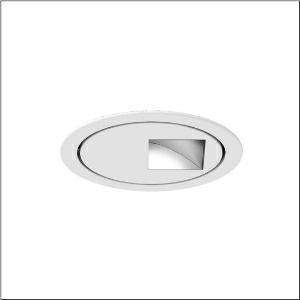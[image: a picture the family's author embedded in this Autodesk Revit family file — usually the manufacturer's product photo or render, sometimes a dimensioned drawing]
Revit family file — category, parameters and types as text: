
# Revit family: lunis_11_mini_round_51dk11b72wn21
name_source: partatom
category: Lighting Fixtures
units: mm (PartAtom-declared; Revit-internal decimal feet)

## family parameters
Cut with Voids When Loaded = No
Host = Face
Light Source = No
Part Type = Normal
Room Calculation Point = No
Round Connector Dimension = Use Diameter
Shared = No

## types (1)
- Lunis 11 mini round (1 x LED 4000K / CRI = 90 (unbekannt), 2120 lm, 4000K)
    Apparent Load = 28 VA
    CIE Flux Codes = 44 77 97 100 100
    Color Rendering = 90
    Color Temperature = 4000K
    Default Elevation = 1800 mm
    Description = Lunis 11 mini round, downlight, light control with wallwasher, of highly reflective aluminium, highly specular, light emission: direct distribution, LED rated luminous flux: 2.120lm, light colour: 940, control gear: ECG, with terminal, 3-pole, mains connection: 220..230V, AC/DC, 0/50..60Hz, LED module, luminaire module, of aluminium, highly specular, white, diameter: 176mm, clamping range: 1..40mm, recessing ring, of plastic, traffic white (RAL 9016), protection rating (complete): IP20, insulation class (complete): insulation class II (safety insulation), certification: CE, permissible ambient temperature for indoor applications: 0..+35°C, packaging unit: 1 piece
    Height = 0 mm  [stored 0 ft]
    Lamp = 1 x LED 4000K / CRI >= 90 (unbekannt)
    Lamp Light Flux = 2120 lm
    Lamp count = 1
    Length = 176 mm
    Luminous efficacy = 75 lm/W
    Manufacturer = Siteco
    ModVariant = No
    Model = 51DK11B72WN21
    Mounting Place = Ceiling
    Mounting Type = Recessed
    Number of Poles = 1
    OnlyDefault = Yes
    Power Factor = 1
    Product Name = Lunis 11 mini round
    Product group = downlight
    ProductGroupID = 401
    Protection Class = Protection class II
    Protection Degree = IP 20
    RLX_Detail_Level = 1
    RLX_Emergency_Light_Flux = 0 lm
    RLX_Emergency_Type = 0
    RLX_Emergency_Type_DB = No
    RlxData = <blob elided: 59237 chars, md5=6d04e144>
    Socket = socket
    Standby Power = 0 W
    System Light Flux = 2120 lm
    System Power = 28 W
    Type Comments = Product without accessories
    Type Image = l_1004772.jpg
    URL = http://relux.com
    VarID = ---
    Voltage = 0 V
    Weight = 0.00 kg
    Width = 176 mm

note: [stored X ft] marks values corroborated as IEEE doubles in the binary element streams (Revit-internal decimal feet)

## geometry (parser evidence)
native form markers: Blend x4, Sweep x11
no freeform markers — native parametric forms only
